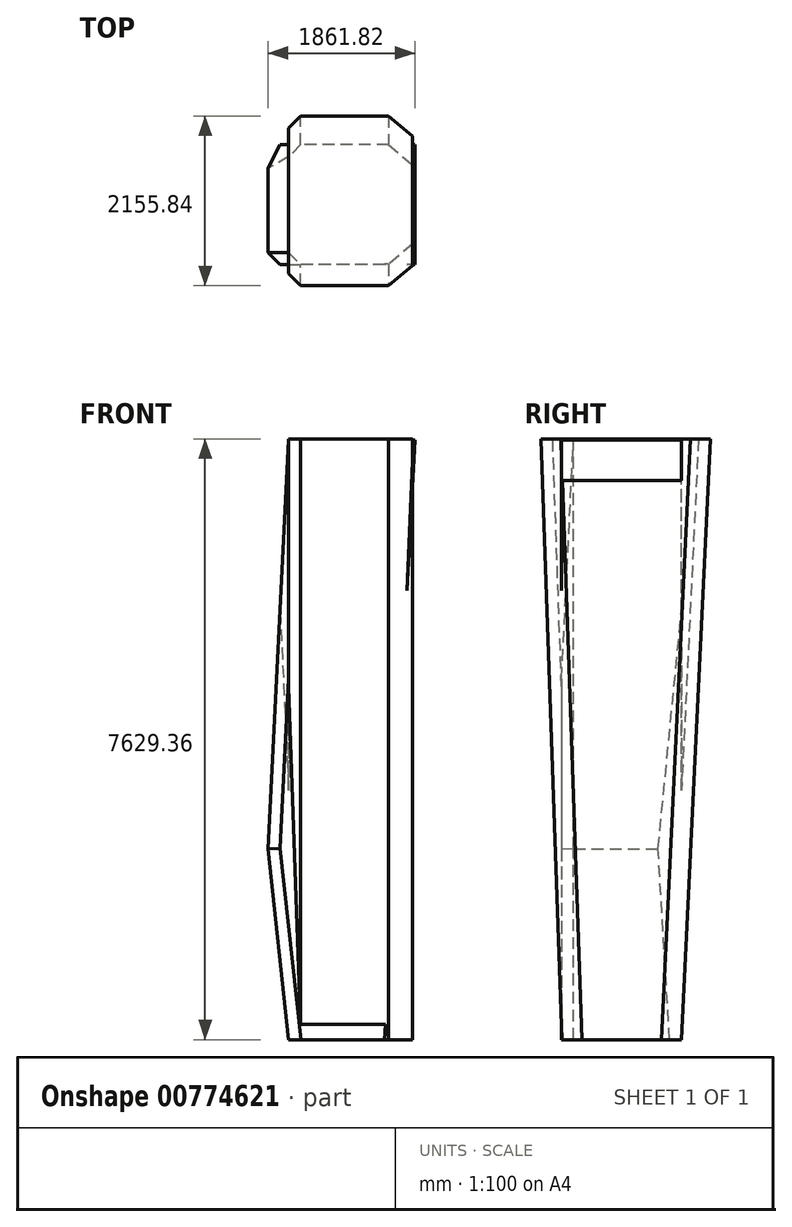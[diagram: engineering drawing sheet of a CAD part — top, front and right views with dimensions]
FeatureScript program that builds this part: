
annotation { "Feature Type Name" : "Feature", "Feature Type Description" : "" }
export const myFeature = defineFeature(function(context is Context, id is Id, definition is map)
    precondition{}
    {
        {
            var Q0;
            Q0=qCreatedBy(makeId("Front.planeOp"),FACE);
            var sketch = newSketch(context, id + "F0", { "sketchPlane" : qUnion([Q0])});
            skLineSegment(sketch, "E0", {"start": v(0, 0) * mm, "end": v(0, 7620) * mm});
            skLineSegment(sketch, "E1", {"start": v(0, 7620) * mm, "end": v(1219.2, 7620) * mm});
            skLineSegment(sketch, "E2", {"start": v(1219.2, 7620) * mm, "end": v(1219.2, 0) * mm});
            skLineSegment(sketch, "E3", {"start": v(1219.2, 0) * mm, "end": v(0, 0) * mm});
            skLineSegment(sketch, "E4", {"start": v(0, 0) * mm, "end": v(-261.02, 2424.39) * mm});
            skLineSegment(sketch, "E5", {"start": v(-261.02, 2424.39) * mm, "end": v(0, 7620) * mm});
            skLineSegment(sketch, "E6", {"start": v(1600.8, 7620) * mm, "end": v(1219.2, 0) * mm});
            skLineSegment(sketch, "E7", {"start": v(1600.8, 7620) * mm, "end": v(1219.2, 7620) * mm});
            skSolve(sketch);
        }
        {
            var Q0;
            Q0 = qSketchRegion(id + "F0", true);
            extrude(context, id + "F1", {"entities" : qUnion([Q0]), "depth" : 1524 * mm, "offsetDistance" : 25.4 * mm});
        }
        {
            var Q0;
            Q0=qCreatedBy(makeId("Right.planeOp"),FACE);
            var sketch = newSketch(context, id + "F2", { "sketchPlane" : qUnion([Q0])});
            skLineSegment(sketch, "E8", {"start": v(0, 0) * mm, "end": v(367.58, 7629.36) * mm});
            skLineSegment(sketch, "E9", {"start": v(367.58, 7629.36) * mm, "end": v(0, 7629.36) * mm});
            skLineSegment(sketch, "E10", {"start": v(0, 7629.36) * mm, "end": v(-1788.26, 7629.36) * mm});
            skLineSegment(sketch, "E11", {"start": v(-1788.26, 7629.36) * mm, "end": v(-1517.09, 0) * mm});
            skLineSegment(sketch, "E12", {"start": v(-1517.09, 0) * mm, "end": v(0, 0) * mm});
            skSolve(sketch);
        }
        {
            var Q0;
            Q0 = qSketchRegion(id + "F2", true);
            extrude(context, id + "F3", {"entities" : qUnion([Q0]), "operationType" : NewBodyOperationType.ADD, "depth" : 1574.8 * mm, "offsetDistance" : 25.4 * mm});
        }
        {
            var Q0;
            Q0=makeQuery(id+"F3.opExtrude","CAP_EDGE",EDGE,{"disambiguationData":[OSD([sQuery(id+"F2.wireOp",EDGE,"E11")])],"isStart":false});
            var Q1;
            Q1=makeQuery(id+"F3.opExtrude","CAP_EDGE",EDGE,{"disambiguationData":[OSD([sQuery(id+"F2.wireOp",EDGE,"E8")])],"isStart":false});
            chamfer(context, id + "F4", {"entities" : qUnion([Q0, Q1]), "chamferType" : ChamferType.TWO_OFFSETS, "width1" : 254 * mm, "oppositeDirection" : false, "width2" : 304.8 * mm, "tangentPropagation" : true});
        }
        {
            var Q0;
            Q0=makeQuery(id+"F3.opExtrude","CAP_EDGE",EDGE,{"disambiguationData":[OSD([sQuery(id+"F2.wireOp",EDGE,"E8")])],"isStart":true});
            chamfer(context, id + "F5", {"entities" : qUnion([Q0]), "width" : 152.4 * mm, "tangentPropagation" : true});
        }
        {
            var Q0;
            Q0=makeQuery(id+"F3.opExtrude","CAP_EDGE",EDGE,{"disambiguationData":[OSD([sQuery(id+"F2.wireOp",EDGE,"E11")])],"isStart":true});
            var Q1;
            Q1=makeQuery(id+"F1.opExtrude","CAP_EDGE",EDGE,{"disambiguationData":[OSD([sQuery(id+"F0.wireOp",EDGE,"E5")])],"isStart":false});
            var Q2;
            Q2=makeQuery(id+"F1.opExtrude","CAP_EDGE",EDGE,{"disambiguationData":[OSD([sQuery(id+"F0.wireOp",EDGE,"E4")])],"isStart":false});
            chamfer(context, id + "F6", {"entities" : qUnion([Q0, Q1, Q2]), "width" : 152.4 * mm, "tangentPropagation" : true});
        }
    });
